# Revit family: Woody
name_source: partatom
category: Мебель
revit_build: Autodesk Revit 2017 (Build: 20160225_1515(x64)
units: mm (PartAtom-declared; Revit-internal decimal feet)

## family parameters
Всегда вертикально = Да
Заголовок OmniClass = General Furniture and Specialties
На основе рабочей плоскости = Нет
Номер OmniClass = 23.40.20.00
Общий = Нет
При загрузке вырезать с полостями = Нет
Точка расчета площади = Нет

## types (3) — shared parameters
Fabric = Skandiform Fabric
Leg = Skandiform wood's book
Изготовитель = Skandiform AB
Ключевая пометка = XBF.2
Комментарии к типоразмеру = Created by Astacus AB
Описание = Stackable chairs in unsteamed beech. Natural or stained. Seat with fixed cover or removable beret cover combined with undercover in rubber webbing.

## per-type parameters (varying)
| type | Backrest | Fabric Seat | URL | Wooden Seat | Группа модели |
| S-077 | Skandiform wood's book | Нет | http://www.biminfo.se | Да | S-077 |
| S-078 | Skandiform wood's book | Да | http://www.biminfo.se | Нет | S-078 |
| S-072 | Skandiform Fabric | Да | http://file-system.ru | Нет | S-078 |

## geometry (parser evidence)
native form markers: Blend x32, Sweep x3
no freeform markers — native parametric forms only
